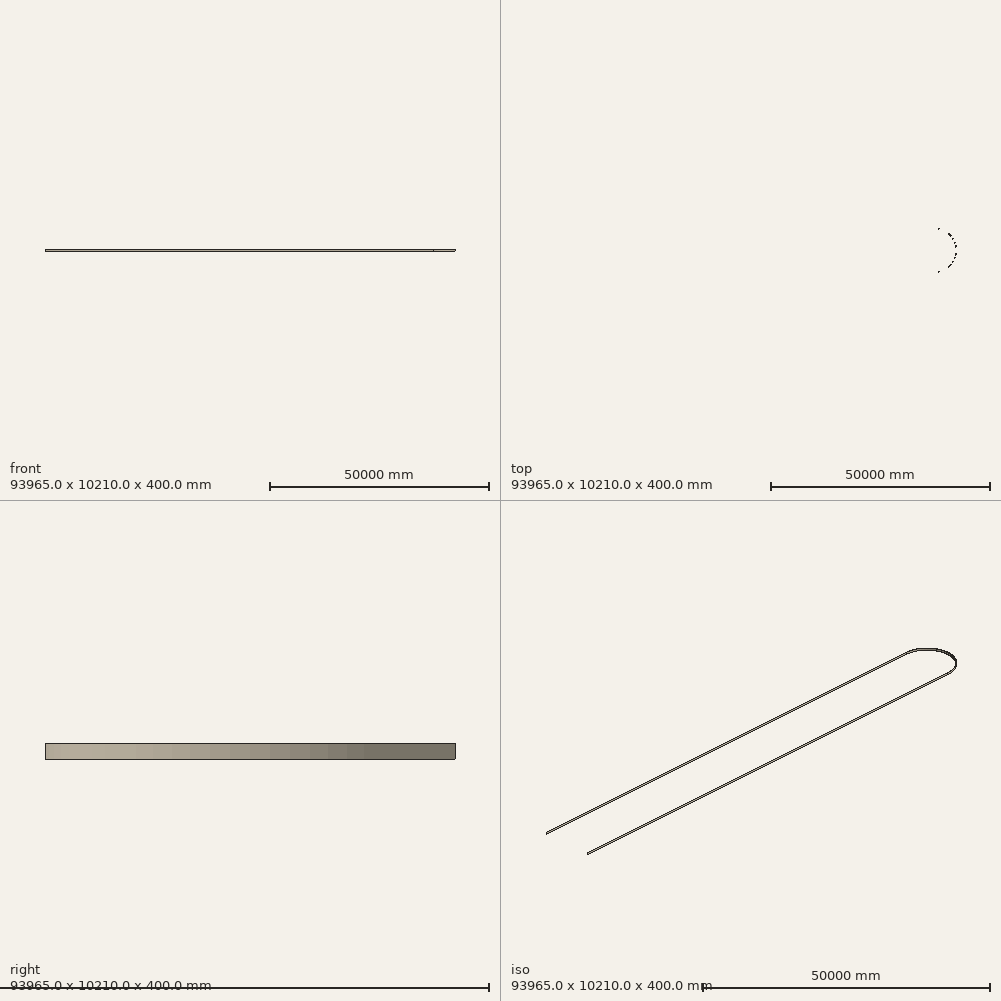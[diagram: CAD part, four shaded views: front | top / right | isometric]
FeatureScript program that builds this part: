
annotation { "Feature Type Name" : "Feature", "Feature Type Description" : "" }
export const myFeature = defineFeature(function(context is Context, id is Id, definition is map)
    precondition{}
    {
        {
            var Q0;
            Q0=qCreatedBy(makeId("Top.planeOp"),FACE);
            var sketch = newSketch(context, id + "F0", { "sketchPlane" : qUnion([Q0])});
            skLineSegment(sketch, "E0.bottom", {"start": v(0, 0) * mm, "end": v(0, 0) * mm});
            skLineSegment(sketch, "E0.top", {"start": v(0, 35) * mm, "end": v(0, 35) * mm});
            skLineSegment(sketch, "E0.left", {"start": v(0, 0) * mm, "end": v(0, 35) * mm});
            skLineSegment(sketch, "E0.right", {"start": v(0, 0) * mm, "end": v(0, 35) * mm});
            skLineSegment(sketch, "E1", {"start": v(0, 35) * mm, "end": v(-88860, 35) * mm});
            skLineSegment(sketch, "E2", {"start": v(0, 0) * mm, "end": v(0, -35) * mm});
            skLineSegment(sketch, "E3", {"start": v(0, -35) * mm, "end": v(-88860, -35) * mm});
            skLineSegment(sketch, "E4", {"start": v(-88860, 5035) * mm, "end": v(0, 5035) * mm});
            skLineSegment(sketch, "E5", {"start": v(-88860, 5035) * mm, "end": v(-88860, 5105) * mm});
            skLineSegment(sketch, "E6", {"start": v(-88860, 5105) * mm, "end": v(0, 5105) * mm});
            skLineSegment(sketch, "E7", {"start": v(-88860, -5035) * mm, "end": v(0, -5035) * mm});
            skLineSegment(sketch, "E8", {"start": v(-88860, -5035) * mm, "end": v(-88860, -5105) * mm});
            skLineSegment(sketch, "E9", {"start": v(-88860, -5105) * mm, "end": v(0, -5105) * mm});
            skArc(sketch, "E10", {"start": v(-88860, 35) * mm, "mid": v(-93895, 5070) * mm, "end": v(-88860, 10105) * mm});
            skArc(sketch, "E11", {"start": v(-88860, -35) * mm, "mid": v(-93895, -5070) * mm, "end": v(-88860, -10105) * mm});
            skLineSegment(sketch, "E12", {"start": v(-88860, 10105) * mm, "end": v(-88860, 10175) * mm, "construction": true});
            skLineSegment(sketch, "E13", {"start": v(-88860, -10105) * mm, "end": v(-88860, -10175) * mm, "construction": true});
            skArc(sketch, "E14", {"start": v(-88860, 10175) * mm, "mid": v(-93956.24, 5368.9) * mm, "end": v(-89456.76, 0) * mm});
            skArc(sketch, "E15", {"start": v(-88860, -10175) * mm, "mid": v(-93956.24, -5368.9) * mm, "end": v(-89456.76, 0) * mm});
            skLineSegment(sketch, "E16", {"start": v(-88860, 10175) * mm, "end": v(0, 10175) * mm});
            skLineSegment(sketch, "E17", {"start": v(-88860, 10105) * mm, "end": v(0, 10105) * mm});
            skLineSegment(sketch, "E18", {"start": v(-88860, -10105) * mm, "end": v(0, -10105) * mm});
            skLineSegment(sketch, "E19", {"start": v(-88860, -10175) * mm, "end": v(0, -10175) * mm});
            skArc(sketch, "E20", {"start": v(0, 5035) * mm, "mid": v(5035, 0) * mm, "end": v(0, -5035) * mm});
            skArc(sketch, "E21", {"start": v(0, 5105) * mm, "mid": v(5105, 0) * mm, "end": v(0, -5105) * mm});
            skArc(sketch, "E22", {"start": v(0, 10105) * mm, "mid": v(10105, 0) * mm, "end": v(0, -10105) * mm});
            skArc(sketch, "E23", {"start": v(0, 10175) * mm, "mid": v(10175, 0) * mm, "end": v(0, -10175) * mm});
            skSolve(sketch);
        }
        {
            var Q0;
            Q0=makeQuery(id+"F0.imprint","IMPRINT",FACE,{"disambiguationData":[TD([[makeQuery(id+"F0.imprint","IMPRINT",EDGE,{"derivedFrom":sQuery(id+"F0.wireOp",EDGE,"E4")}),1.0]])]});
            var Q1;
            Q1=makeQuery(id+"F0.imprint","IMPRINT",FACE,{"disambiguationData":[TD([[makeQuery(id+"F0.imprint","IMPRINT",EDGE,{"derivedFrom":sQuery(id+"F0.wireOp",EDGE,"E0.right")}),-1.0]])]});
            var Q2;
            Q2=makeQuery(id+"F0.imprint","IMPRINT",FACE,{"disambiguationData":[TD([[makeQuery(id+"F0.imprint","IMPRINT",EDGE,{"derivedFrom":sQuery(id+"F0.wireOp",EDGE,"E0.right")}),1.0]])]});
            extrude(context, id + "F1", {"entities" : qUnion([Q0, Q1, Q2]), "oppositeDirection" : true, "depth" : 50 * mm});
        }
        {
            var Q0;
            Q0=makeQuery(id+"F0.imprint","IMPRINT",FACE,{"disambiguationData":[TD([[makeQuery(id+"F0.imprint","IMPRINT",EDGE,{"derivedFrom":sQuery(id+"F0.wireOp",EDGE,"E0.right")}),1.0]])]});
            var Q1;
            Q1=makeQuery(id+"F0.imprint","IMPRINT",FACE,{"disambiguationData":[TD([[makeQuery(id+"F0.imprint","IMPRINT",EDGE,{"derivedFrom":sQuery(id+"F0.wireOp",EDGE,"E4")}),1.0]])]});
            extrude(context, id + "F2", {"entities" : qUnion([Q0, Q1]), "operationType" : NewBodyOperationType.ADD, "depth" : 350 * mm});
        }
    });
